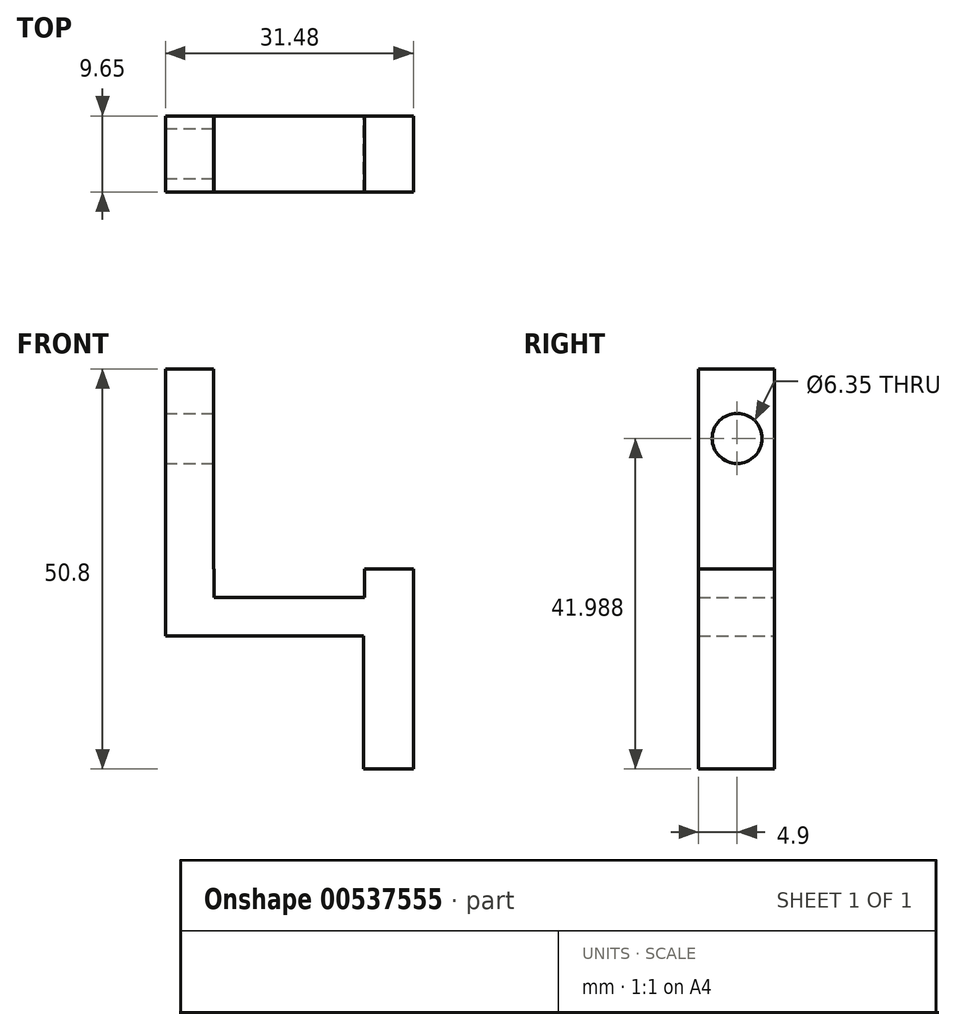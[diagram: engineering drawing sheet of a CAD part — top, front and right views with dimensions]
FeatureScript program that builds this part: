
annotation { "Feature Type Name" : "Feature", "Feature Type Description" : "" }
export const myFeature = defineFeature(function(context is Context, id is Id, definition is map)
    precondition{}
    {
        {
            var Q0;
            Q0=qCreatedBy(makeId("Front.planeOp"),FACE);
            var sketch = newSketch(context, id + "F0", { "sketchPlane" : qUnion([Q0])});
            skLineSegment(sketch, "E0", {"start": v(-44.8, 40.7) * mm, "end": v(-44.8, 15.3) * mm});
            skLineSegment(sketch, "E1", {"start": v(-44.8, 15.3) * mm, "end": v(-19.4, 15.3) * mm});
            skLineSegment(sketch, "E2", {"start": v(-19.4, 15.3) * mm, "end": v(-19.4, -10.1) * mm});
            skLineSegment(sketch, "E3", {"start": v(-19.4, -10.1) * mm, "end": v(-25.75, -10.1) * mm});
            skLineSegment(sketch, "E4", {"start": v(-25.75, -10.1) * mm, "end": v(-25.75, 6.82) * mm});
            skLineSegment(sketch, "E5", {"start": v(-25.75, 6.82) * mm, "end": v(-50.88, 6.82) * mm});
            skLineSegment(sketch, "E6", {"start": v(-50.88, 6.82) * mm, "end": v(-50.88, 40.7) * mm});
            skLineSegment(sketch, "E7", {"start": v(-44.8, 40.7) * mm, "end": v(-50.88, 40.7) * mm});
            skSolve(sketch);
        }
        {
            var Q0;
            Q0=qSketchRegion(id+"F0",true);
            extrude(context, id + "F1", {"entities" : qUnion([Q0]), "depth" : 9.65 * mm, "offsetDistance" : 25.4 * mm});
        }
        {
            var Q0;
            Q0=makeQuery(id+"F1.opExtrude","SWEPT_FACE",FACE,{"disambiguationData":[OSD([sQuery(id+"F0.wireOp",EDGE,"E2")])]});
            var sketch = newSketch(context, id + "F2", { "sketchPlane" : qUnion([Q0])});
            skCircle(sketch, "E8", {"center": v(-4.97, -3.57) * mm, "radius": 2.2 * mm});
            skSolve(sketch);
        }
        {
            var Q0;
            Q0=qCreatedBy(makeId("Right.planeOp"),FACE);
            var sketch = newSketch(context, id + "F3", { "sketchPlane" : qUnion([Q0])});
            skCircle(sketch, "E9", {"center": v(-4.75, 31.89) * mm, "radius": 3.18 * mm});
            skSolve(sketch);
        }
        {
            var Q0;
            Q0=makeQuery(id+"F3.imprint","IMPRINT",FACE,{"disambiguationData":[TD([[makeQuery(id+"F3.imprint","IMPRINT",EDGE,{"derivedFrom":sQuery(id+"F3.wireOp",EDGE,"E9")}),1.0]])]});
            extrude(context, id + "F4", {"entities" : qUnion([Q0]), "operationType" : NewBodyOperationType.REMOVE, "oppositeDirection" : true, "depth" : 55.88 * mm, "offsetDistance" : 25.4 * mm});
        }
        {
            var Q0;
            Q0=qCreatedBy(makeId("Front.planeOp"),FACE);
            var sketch = newSketch(context, id + "F5", { "sketchPlane" : qUnion([Q0])});
            skLineSegment(sketch, "E10", {"start": v(-44.72, 14.22) * mm, "end": v(-44.72, 11.68) * mm});
            skLineSegment(sketch, "E11", {"start": v(-44.72, 11.68) * mm, "end": v(-25.6, 11.68) * mm});
            skLineSegment(sketch, "E12", {"start": v(-25.6, 11.68) * mm, "end": v(-25.6, 14.22) * mm});
            skLineSegment(sketch, "E13", {"start": v(-25.6, 14.22) * mm, "end": v(-44.72, 14.22) * mm});
            skLineSegment(sketch, "E14", {"start": v(-44.72, 14.22) * mm, "end": v(-44.72, 15.51) * mm});
            skLineSegment(sketch, "E15", {"start": v(-44.72, 15.51) * mm, "end": v(-25.6, 15.51) * mm});
            skLineSegment(sketch, "E16", {"start": v(-25.6, 14.22) * mm, "end": v(-25.6, 15.51) * mm});
            skSolve(sketch);
        }
        {
            var Q0;
            Q0 = qSketchRegion(id + "F5", true);
            extrude(context, id + "F6", {"entities" : qUnion([Q0]), "operationType" : NewBodyOperationType.REMOVE, "depth" : 25.4 * mm, "offsetDistance" : 25.4 * mm});
        }
    });
